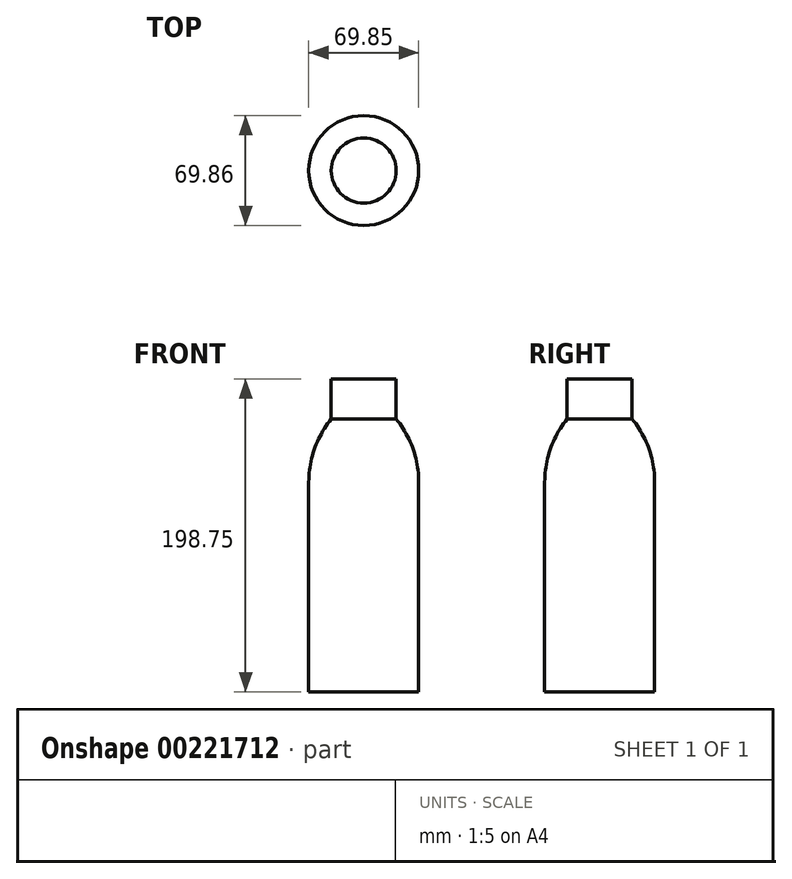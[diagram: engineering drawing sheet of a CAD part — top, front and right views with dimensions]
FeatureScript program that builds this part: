
annotation { "Feature Type Name" : "Feature", "Feature Type Description" : "" }
export const myFeature = defineFeature(function(context is Context, id is Id, definition is map)
    precondition{}
    {
        {
            var Q0;
            Q0=qCreatedBy(makeId("Front.planeOp"),FACE);
            var sketch = newSketch(context, id + "F0", { "sketchPlane" : qUnion([Q0])});
            skLineSegment(sketch, "E0", {"start": v(4.26, 105.35) * mm, "end": v(24.9, 105.35) * mm});
            skLineSegment(sketch, "E1.MirrorCS", {"start": v(24.9, 105.35) * mm, "end": v(24.9, -93.4) * mm});
            skLineSegment(sketch, "E2.MirrorCS", {"start": v(-10.03, -93.4) * mm, "end": v(-10.03, 39.95) * mm});
            skArc(sketch, "E3.MirrorCS", {"start": v(-10.03, 39.95) * mm, "mid": v(-6.35, 61.19) * mm, "end": v(4.26, 79.95) * mm});
            skLineSegment(sketch, "E4.MirrorCS", {"start": v(4.26, 79.95) * mm, "end": v(4.26, 105.35) * mm});
            skLineSegment(sketch, "E5.MirrorCS", {"start": v(24.9, -93.4) * mm, "end": v(-10.03, -93.4) * mm});
            skSolve(sketch);
        }
        {
            var Q0;
            Q0=makeQuery(id+"F0.imprint","IMPRINT",FACE,{"disambiguationData":[TD([[makeQuery(id+"F0.imprint","IMPRINT",EDGE,{"derivedFrom":sQuery(id+"F0.wireOp",EDGE,"E0")}),-1.0]])]});
            var Q1;
            Q1=sQuery(id+"F0.wireOp",EDGE,"E1.MirrorCS");
            revolve(context, id + "F1", {"entities" : qUnion([Q0]), "axis" : qUnion([Q1]), "revolveType" : RevolveType.FULL});
        }
    });
